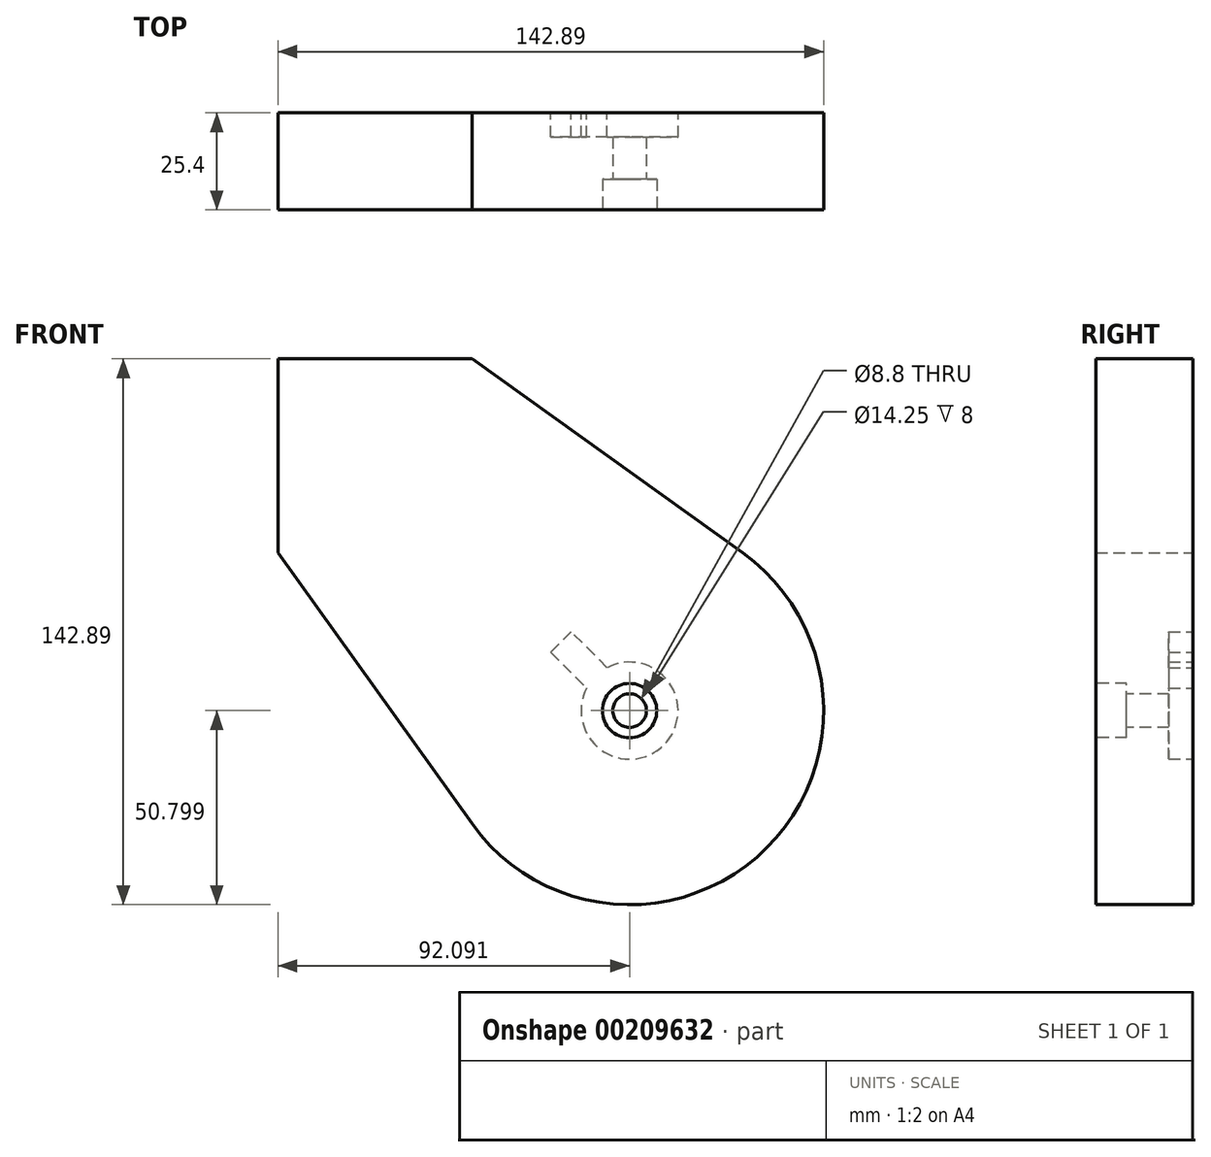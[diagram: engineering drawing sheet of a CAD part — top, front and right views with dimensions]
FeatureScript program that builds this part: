
annotation { "Feature Type Name" : "Feature", "Feature Type Description" : "" }
export const myFeature = defineFeature(function(context is Context, id is Id, definition is map)
    precondition{}
    {
        {
            var Q0;
            Q0=qCreatedBy(makeId("Front.planeOp"),FACE);
            var sketch = newSketch(context, id + "F0", { "sketchPlane" : qUnion([Q0])});
            skLineSegment(sketch, "E0", {"start": v(-50.8, 0) * mm, "end": v(-50.8, 50.8) * mm});
            skLineSegment(sketch, "E1", {"start": v(-50.8, 50.8) * mm, "end": v(0, 50.8) * mm});
            skLineSegment(sketch, "E2", {"start": v(0, 50.8) * mm, "end": v(70.88, 0) * mm});
            skLineSegment(sketch, "E3", {"start": v(-50.8, 0) * mm, "end": v(0, -70.88) * mm});
            skArc(sketch, "E4", {"start": v(70.88, 0) * mm, "mid": v(77.21, -77.21) * mm, "end": v(0, -70.88) * mm});
            skSolve(sketch);
        }
        {
            var Q0;
            Q0 = qSketchRegion(id + "F0", true);
            extrude(context, id + "F1", {"entities" : qUnion([Q0]), "depth" : 25.4 * mm});
        }
        {
            var Q0;
            Q0=makeQuery(id+"F1.opExtrude","CAP_FACE",FACE,{"disambiguationData":[OSD([sQuery(id+"F0.wireOp",EDGE,"E0"),sQuery(id+"F0.wireOp",EDGE,"E1"),sQuery(id+"F0.wireOp",EDGE,"E2"),sQuery(id+"F0.wireOp",EDGE,"E3"),sQuery(id+"F0.wireOp",EDGE,"E4")])],"isStart":false});
            var sketch = newSketch(context, id + "F2", { "sketchPlane" : qUnion([Q0])});
            skPoint(sketch, "E5", {"position": v(41.3, -41.3) * mm});
            skSolve(sketch);
        }
        {
            var Q0;
            Q0=sQuery(id+"F2.wireOp",VERTEX,"E5");
            var Q1;
            Q1=makeQuery(id+"F1.opExtrude","SWEPT_BODY",BODY,{"disambiguationData":[OSD([sQuery(id+"F0.wireOp",EDGE,"E0"),sQuery(id+"F0.wireOp",EDGE,"E1"),sQuery(id+"F0.wireOp",EDGE,"E2"),sQuery(id+"F0.wireOp",EDGE,"E3"),sQuery(id+"F0.wireOp",EDGE,"E4")])]});
            hole(context, id + "F3", {"style" : HoleStyle.C_BORE, "endStyle" : HoleEndStyle.THROUGH, "standardTappedOrClearance" : lookupTablePath({ "standard" : "ISO", "fit" : "Normal", "size" : "M8", "type" : "Clearance" }), "standardBlindInLast" : lookupTablePath({ "fit" : "Standard", "standard" : "ISO", "size" : "M8", "type" : "Clearance" }), "holeDiameter" : 8.8 * mm, "cBoreDiameter" : 14.25 * mm, "cBoreDepth" : 8 * mm, "locations" : qUnion([Q0]), "scope" : qUnion([Q1]), "isTappedThrough" : true});
        }
        {
            var Q0;
            Q0=makeQuery(id+"F1.opExtrude","CAP_FACE",FACE,{"disambiguationData":[OSD([sQuery(id+"F0.wireOp",EDGE,"E0"),sQuery(id+"F0.wireOp",EDGE,"E1"),sQuery(id+"F0.wireOp",EDGE,"E2"),sQuery(id+"F0.wireOp",EDGE,"E3"),sQuery(id+"F0.wireOp",EDGE,"E4")])],"isStart":true});
            var sketch = newSketch(context, id + "F4", { "sketchPlane" : qUnion([Q0])});
            skCircle(sketch, "E6", {"center": v(-41.3, -41.3) * mm, "radius": 12.7 * mm});
            skLineSegment(sketch, "E7", {"start": v(-41.3, -41.3) * mm, "end": v(50.8, 50.8) * mm, "construction": true});
            skLineSegment(sketch, "E8", {"start": v(-26.02, -20.64) * mm, "end": v(-20.64, -26.02) * mm});
            skLineSegment(sketch, "E9", {"start": v(-20.64, -26.02) * mm, "end": v(-38.6, -43.99) * mm});
            skLineSegment(sketch, "E10", {"start": v(-38.6, -43.99) * mm, "end": v(-43.99, -38.6) * mm});
            skLineSegment(sketch, "E11", {"start": v(-43.99, -38.6) * mm, "end": v(-26.02, -20.64) * mm});
            skSolve(sketch);
        }
        {
            var Q0;
            Q0 = qSketchRegion(id + "F4", true);
            extrude(context, id + "F5", {"entities" : qUnion([Q0]), "operationType" : NewBodyOperationType.REMOVE, "oppositeDirection" : true, "depth" : 6.35 * mm});
        }
    });
